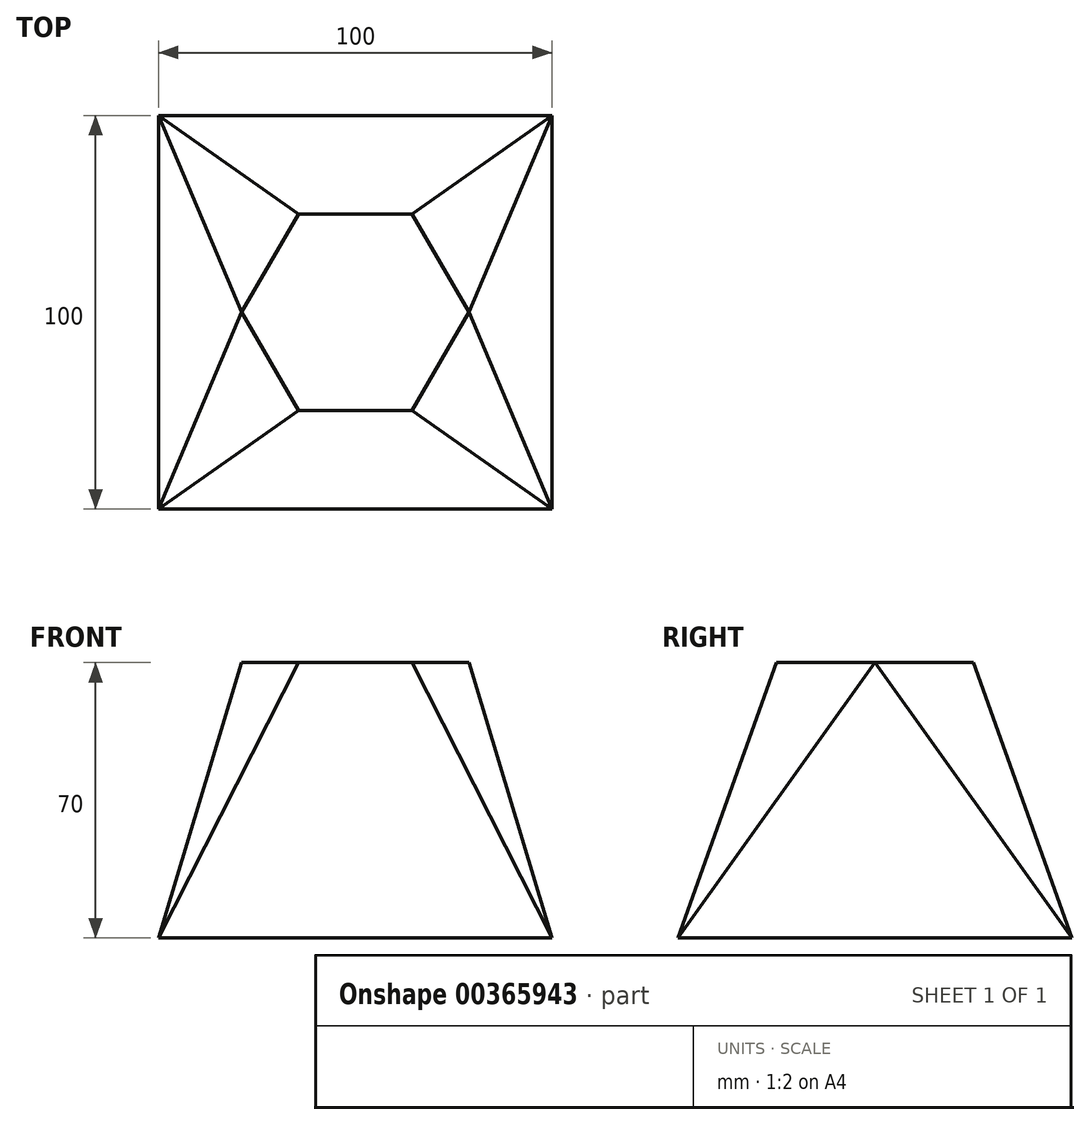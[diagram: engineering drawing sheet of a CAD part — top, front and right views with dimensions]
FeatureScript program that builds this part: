
annotation { "Feature Type Name" : "Feature", "Feature Type Description" : "" }
export const myFeature = defineFeature(function(context is Context, id is Id, definition is map)
    precondition{}
    {
        {
            var Q0;
            Q0=qCreatedBy(makeId("Top.planeOp"),FACE);
            var sketch = newSketch(context, id + "F0", { "sketchPlane" : qUnion([Q0])});
            skLineSegment(sketch, "E0.bottom", {"start": v(50, -50) * mm, "end": v(-50, -50) * mm});
            skLineSegment(sketch, "E0.top", {"start": v(50, 50) * mm, "end": v(-50, 50) * mm});
            skLineSegment(sketch, "E0.left", {"start": v(50, -50) * mm, "end": v(50, 50) * mm});
            skLineSegment(sketch, "E0.right", {"start": v(-50, -50) * mm, "end": v(-50, 50) * mm});
            skPoint(sketch, "E0.middle", {"position": v(0, 0) * mm});
            skSolve(sketch);
        }
        {
            var Q0;
            Q0=makeQuery(id+"F0.imprint","IMPRINT",FACE,{"disambiguationData":[TD([[makeQuery(id+"F0.imprint","IMPRINT",EDGE,{"derivedFrom":sQuery(id+"F0.wireOp",EDGE,"E0.bottom")}),-1.0]])]});
            cPlane(context, id + "F1", {"entities" : qUnion([Q0]), "cplaneType" : CPlaneType.OFFSET, "offset" : 70 * mm, "width" : 150 * mm, "height" : 150 * mm});
        }
        {
            var Q0;
            Q0=qCreatedBy(id+"F1.planeOp",FACE);
            var sketch = newSketch(context, id + "F2", { "sketchPlane" : qUnion([Q0])});
            skCircle(sketch, "E1.cCircle", {"center": v(0, 0) * mm, "radius": 25 * mm, "construction": true});
            skLineSegment(sketch, "E1.0", {"start": v(28.87, 0) * mm, "end": v(14.43, -25) * mm});
            skLineSegment(sketch, "E1.1", {"start": v(14.43, -25) * mm, "end": v(-14.43, -25) * mm});
            skLineSegment(sketch, "E1.2", {"start": v(-14.43, -25) * mm, "end": v(-28.87, 0) * mm});
            skLineSegment(sketch, "E1.3", {"start": v(-28.87, 0) * mm, "end": v(-14.43, 25) * mm});
            skLineSegment(sketch, "E1.4", {"start": v(-14.43, 25) * mm, "end": v(14.43, 25) * mm});
            skLineSegment(sketch, "E1.5", {"start": v(14.43, 25) * mm, "end": v(28.87, 0) * mm});
            skPoint(sketch, "E1.0.midPoint", {"position": v(21.65, -12.5) * mm});
            skLineSegment(sketch, "E2", {"start": v(-14.43, 25) * mm, "end": v(-14.43, -25) * mm});
            skLineSegment(sketch, "E3", {"start": v(14.43, 25) * mm, "end": v(14.43, -25) * mm});
            skSolve(sketch);
        }
        {
            var Q0;
            Q0=makeQuery(id+"F2.imprint","IMPRINT",FACE,{"disambiguationData":[TD([[makeQuery(id+"F2.imprint","IMPRINT",EDGE,{"derivedFrom":sQuery(id+"F2.wireOp",EDGE,"E1.1")}),-1.0]])]});
            var Q1;
            Q1=makeQuery(id+"F0.imprint","IMPRINT",FACE,{"disambiguationData":[TD([[makeQuery(id+"F0.imprint","IMPRINT",EDGE,{"derivedFrom":sQuery(id+"F0.wireOp",EDGE,"E0.bottom")}),-1.0]])]});
            loft(context, id + "F3", {"sheetProfilesArray" : [{ "sheetProfileEntities" : qUnion([Q0]) }, { "sheetProfileEntities" : qUnion([Q1]) }]});
        }
        {
            var Q1;
            Q1=sQuery(id+"F2.wireOp",VERTEX,"E1.3.start");
            var Q2;
            Q2=makeQuery(id+"F3.opLoft","SWEPT_FACE",FACE,{"disambiguationData":[OSD([sQuery(id+"F0.wireOp",EDGE,"E0.bottom"),sQuery(id+"F0.wireOp",EDGE,"E0.top"),sQuery(id+"F0.wireOp",EDGE,"E0.right"),sQuery(id+"F2.wireOp",EDGE,"E1.1"),sQuery(id+"F2.wireOp",EDGE,"E1.2"),sQuery(id+"F2.wireOp",EDGE,"E1.3"),sQuery(id+"F2.wireOp",EDGE,"E1.4"),sQuery(id+"F2.wireOp",EDGE,"E2")])]});
            loft(context, id + "F4", {"operationType" : NewBodyOperationType.ADD, "sheetProfilesArray" : [{ "sheetProfileEntities" : qUnion([Q1]) }, { "sheetProfileEntities" : qUnion([Q2]) }]});
        }
        {
            var Q1;
            Q1=sQuery(id+"F2.wireOp",VERTEX,"E1.0.start");
            var Q2;
            Q2=makeQuery(id+"F3.opLoft","SWEPT_FACE",FACE,{"disambiguationData":[OSD([sQuery(id+"F0.wireOp",EDGE,"E0.bottom"),sQuery(id+"F0.wireOp",EDGE,"E0.top"),sQuery(id+"F0.wireOp",EDGE,"E0.left"),sQuery(id+"F2.wireOp",EDGE,"E1.0"),sQuery(id+"F2.wireOp",EDGE,"E1.1"),sQuery(id+"F2.wireOp",EDGE,"E1.4"),sQuery(id+"F2.wireOp",EDGE,"E1.5"),sQuery(id+"F2.wireOp",EDGE,"E3")])]});
            loft(context, id + "F5", {"operationType" : NewBodyOperationType.ADD, "sheetProfilesArray" : [{ "sheetProfileEntities" : qUnion([Q1]) }, { "sheetProfileEntities" : qUnion([Q2]) }]});
        }
    });
